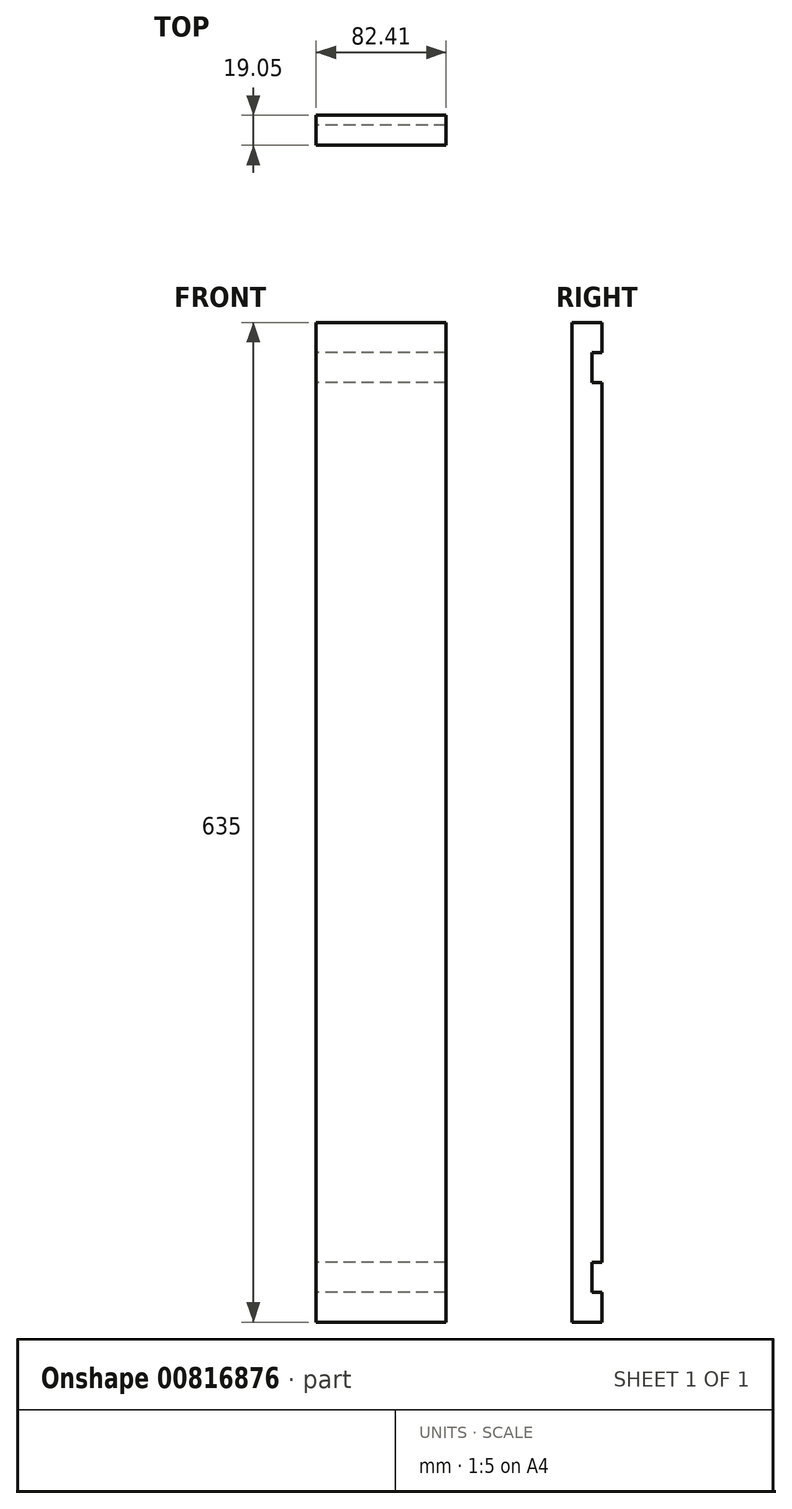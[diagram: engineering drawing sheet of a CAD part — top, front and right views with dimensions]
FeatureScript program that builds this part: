
annotation { "Feature Type Name" : "Feature", "Feature Type Description" : "" }
export const myFeature = defineFeature(function(context is Context, id is Id, definition is map)
    precondition{}
    {
        {
            var Q0;
            Q0=qCreatedBy(makeId("Front.planeOp"),FACE);
            var sketch = newSketch(context, id + "F0", { "sketchPlane" : qUnion([Q0])});
            skLineSegment(sketch, "E0.bottom", {"start": v(82.4, -635) * mm, "end": v(0, -635) * mm});
            skLineSegment(sketch, "E0.top", {"start": v(82.4, 0) * mm, "end": v(0, 0) * mm});
            skLineSegment(sketch, "E0.left", {"start": v(82.4, -635) * mm, "end": v(82.4, 0) * mm});
            skLineSegment(sketch, "E0.right", {"start": v(0, -635) * mm, "end": v(0, 0) * mm});
            skSolve(sketch);
        }
        {
            var Q0;
            Q0 = qSketchRegion(id + "F0", true);
            extrude(context, id + "F1", {"entities" : qUnion([Q0]), "depth" : 19.05 * mm, "offsetDistance" : 25.4 * mm});
        }
        {
            var Q0;
            Q0=makeQuery(id+"F1.opExtrude","SWEPT_FACE",FACE,{"disambiguationData":[OSD([sQuery(id+"F0.wireOp",EDGE,"E0.right")])]});
            var sketch = newSketch(context, id + "F2", { "sketchPlane" : qUnion([Q0])});
            skLineSegment(sketch, "E1.bottom", {"start": v(0, -19.05) * mm, "end": v(6.35, -19.05) * mm});
            skLineSegment(sketch, "E1.top", {"start": v(0, -38.1) * mm, "end": v(6.35, -38.1) * mm});
            skLineSegment(sketch, "E1.left", {"start": v(0, -19.05) * mm, "end": v(0, -38.1) * mm});
            skLineSegment(sketch, "E1.right", {"start": v(6.35, -19.05) * mm, "end": v(6.35, -38.1) * mm});
            skLineSegment(sketch, "E2.bottom", {"start": v(0, -596.9) * mm, "end": v(6.35, -596.9) * mm});
            skLineSegment(sketch, "E2.top", {"start": v(0, -615.95) * mm, "end": v(6.35, -615.95) * mm});
            skLineSegment(sketch, "E2.left", {"start": v(0, -596.9) * mm, "end": v(0, -615.95) * mm});
            skLineSegment(sketch, "E2.right", {"start": v(6.35, -596.9) * mm, "end": v(6.35, -615.95) * mm});
            skSolve(sketch);
        }
        {
            var Q0;
            Q0 = qSketchRegion(id + "F2", true);
            extrude(context, id + "F3", {"entities" : qUnion([Q0]), "operationType" : NewBodyOperationType.REMOVE, "endBound" : BoundingType.THROUGH_ALL, "oppositeDirection" : true, "depth" : 25.4 * mm, "offsetDistance" : 25.4 * mm});
        }
    });
